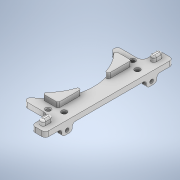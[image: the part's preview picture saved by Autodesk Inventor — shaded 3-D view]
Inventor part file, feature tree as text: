
AUTODESK INVENTOR PART (.ipt)
format: ipt  version: 2022 (Build 260153000, 153)  size: 4,649,984 bytes
history: native  units: in
note: dims shown in document units (in); Inventor stores cm internally (conversion verified against a paired STEP export)
features: sketch x14, extrude x9, fillet x9, hole x3, mirror x2, chamfer x2, plane x1, sweep x1
ambient origin geometry x8: Origin, YZ Plane, XZ Plane, XY Plane, X Axis, Y Axis, Z Axis, Center Point
bodies: Solid1 (feature_tree)
feature tree (41):
  extrude  "Extrusion1"  Depth=2.811in
  extrude  "Extrusion2"  Depth=0.1181in
  hole  "Hole1"  [1 undecoded]
  extrude  "Extrusion3"  Depth=0.1181in
  fillet  "Fillet1"  Radius=0.1181in
  fillet  "Fillet2"  Radius=0.376in
  fillet  "Fillet6"  Radius=0.1181in
  plane  "Work Plane1"
  mirror  "Mirror1"
  extrude  "Extrusion9"  Depth=0.1181in TaperAngle=0.0deg
  sweep  "Sweep5"
  extrude  "Extrusion10"  Depth=0.1181in
  extrude  "Extrusion11"  Depth=0.1181in
  fillet  "Fillet11"  Radius=0.1181in
  mirror  "Mirror2"
  fillet  "Fillet12"  Radius=2.2677in
  hole  "Hole4"  [1 undecoded]
  chamfer  "Chamfer3"  Distance=1.4055in
  extrude  "Extrusion12"  Depth=0.0394in
  fillet  "Fillet13"  Radius=2.5433in
  fillet  "Fillet14"  Radius=1.5748in
  hole  "Hole5"  [1 undecoded]
  chamfer  "Chamfer4"  Distance=0.3022in
  extrude  "Extrusion13"  Depth=0.0394in
  fillet  "Fillet15"  Radius=0.0992in
  extrude  "Extrusion14"  Depth=0.0394in TaperAngle=0.0deg
  fillet  "Fillet16"  Radius=0.0197in
  sketch  "Sketch1"  dims[d0=0.315in d1=2.811in]
  sketch  "Sketch2"  dims[d2=0.1181in d3=0.0in d7=0.1181in]
  sketch  "Sketch3"  dims[d8=0.1181in d9=0.1102in]
  sketch  "Sketch4"  dims[d10=0.0669in d13=1.4055in d14=0.1181in d15=0.376in d16=0.1181in]
  sketch  "Sketch15"  dims[d17=0.7874in d19=360.0deg d21=0.1181in d22=0.0in]
  sketch  "Sketch17"  dims[d23=0.124in d24=0.2362in d25=0.1575in d26=0.0787in d27=90.0deg d28=0.315in d29=0.8108in d30=0.1181in]
  sketch  "3D Sketch4"
  sketch  "Sketch18"  dims[d31=0.378in d32=0.1181in]
  sketch  "Sketch19"  dims[d33=0.378in d34=0.1181in d35=0.1181in d38=2.2677in]
  sketch  "Sketch20"  dims[d39=180.0deg d41=0.1181in d42=0.0in]
  sketch  "Sketch21"  dims[d43=0.0787in]
  sketch  "Sketch22"  dims[d52=0.1181in]
  sketch  "Sketch23"  dims[d81=0.0394in]
  sketch  "Sketch25"  dims[d126=1.1811in d127=1.4055in d128=2.1654in d134=2.5433in d135=1.5748in d137=0.3022in d138=0.3022in d139=0.0992in d140=0.0992in d141=0.2165in d142=0.0in d151=0.0197in d152=0.1417in d153=0.0374in d154=0.0in d155=0.0in d157=0.2165in d158=0.2165in d159=0.1575in d160=0.0in d161=0.0787in d162=0.1969in d163=0.0in d164=0.0in d165=0.0787in d166=0.0394in d167=0.1018in d168=0.437in d169=0.437in d171=0.1018in d172=0.0866in d173=0.2362in d174=0.1575in d175=0.0787in d176=90.0deg d177=0.315in d178=0.8108in d179=0.0197in d180=0.0787in d181=45.0deg d182=0.2441in d183=0.3813in d188=0.1348in d189=0.0in d194=0.1654in d195=0.0in d196=0.0709in d197=0.2441in d198=0.3813in d199=0.1348in d200=0.0709in d201=0.0512in d202=0.0827in d203=0.0512in d204=0.0827in d205=0.0866in d206=0.2362in d207=0.1575in d208=0.0787in d209=90.0deg d210=0.315in d211=0.8108in d212=0.0197in d213=0.0787in d214=45.0deg d215=0.1831in d216=0.1831in d217=0.1654in d218=0.0in d219=0.0197in d220=0.4134in d221=0.5906in d222=0.2323in d223=0.3386in d224=0.1181in d225=0.0in d227=0.0394in]
note: 3 required parameter values undecoded (feature->parameter linkage not recoverable at this tier; creation-order binding heuristic only, values carry confidence <= 0.55)
